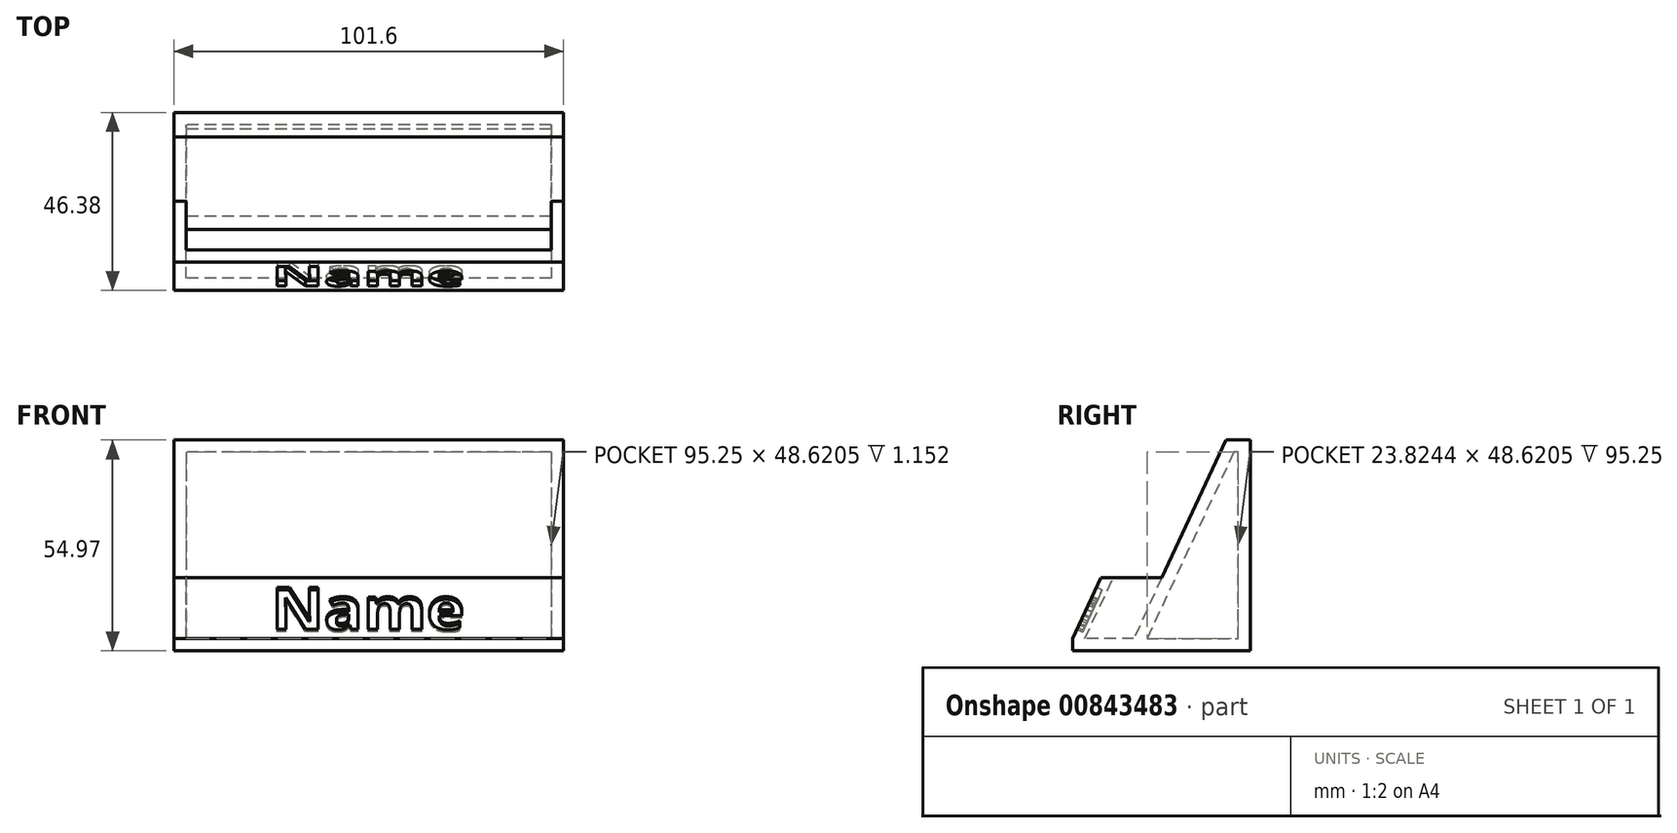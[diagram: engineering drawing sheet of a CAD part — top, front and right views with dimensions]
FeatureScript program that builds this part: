
annotation { "Feature Type Name" : "Feature", "Feature Type Description" : "" }
export const myFeature = defineFeature(function(context is Context, id is Id, definition is map)
    precondition{}
    {
        {
            var Q0;
            Q0=qCreatedBy(makeId("Right.planeOp"),FACE);
            var sketch = newSketch(context, id + "F0", { "sketchPlane" : qUnion([Q0])});
            skLineSegment(sketch, "E0", {"start": v(0, 0) * mm, "end": v(46.38, 0) * mm});
            skLineSegment(sketch, "E1", {"start": v(46.38, 0) * mm, "end": v(46.38, 54.97) * mm});
            skLineSegment(sketch, "E2", {"start": v(46.38, 54.97) * mm, "end": v(40.03, 54.97) * mm});
            skLineSegment(sketch, "E3", {"start": v(40.03, 54.97) * mm, "end": v(15.88, 3.17) * mm});
            skLineSegment(sketch, "E4", {"start": v(15.88, 3.17) * mm, "end": v(3.18, 3.17) * mm});
            skLineSegment(sketch, "E5", {"start": v(3.17, 3.17) * mm, "end": v(10.58, 19.05) * mm});
            skLineSegment(sketch, "E6", {"start": v(0, 0) * mm, "end": v(0, 3.17) * mm});
            skLineSegment(sketch, "E7", {"start": v(0, 3.17) * mm, "end": v(7.4, 19.05) * mm});
            skLineSegment(sketch, "E8", {"start": v(7.4, 19.05) * mm, "end": v(10.58, 19.05) * mm});
            skLineSegment(sketch, "E9.0", {"start": v(42.05, 51.8) * mm, "end": v(19.38, 3.17) * mm});
            skLineSegment(sketch, "E9.1", {"start": v(43.2, 51.8) * mm, "end": v(42.05, 51.8) * mm});
            skLineSegment(sketch, "E9.2", {"start": v(43.2, 3.17) * mm, "end": v(43.2, 51.8) * mm});
            skLineSegment(sketch, "E9.3", {"start": v(19.38, 3.17) * mm, "end": v(43.2, 3.17) * mm});
            skSolve(sketch);
        }
        {
            var Q0;
            Q0 = qSketchRegion(id + "F0", true);
            extrude(context, id + "F1", {"entities" : qUnion([Q0]), "endBound" : BoundingType.SYMMETRIC, "depth" : 95.25 * mm, "offsetDistance" : 25.4 * mm});
        }
        {
            var Q0;
            Q0=makeQuery(id+"F1.opExtrude","CAP_FACE",FACE,{"disambiguationData":[OSD([sQuery(id+"F0.wireOp",EDGE,"E0"),sQuery(id+"F0.wireOp",EDGE,"E1"),sQuery(id+"F0.wireOp",EDGE,"E2"),sQuery(id+"F0.wireOp",EDGE,"E3"),sQuery(id+"F0.wireOp",EDGE,"E4"),sQuery(id+"F0.wireOp",EDGE,"E5"),sQuery(id+"F0.wireOp",EDGE,"E6"),sQuery(id+"F0.wireOp",EDGE,"E7"),sQuery(id+"F0.wireOp",EDGE,"E8"),sQuery(id+"F0.wireOp",EDGE,"E9.0"),sQuery(id+"F0.wireOp",EDGE,"E9.1"),sQuery(id+"F0.wireOp",EDGE,"E9.2"),sQuery(id+"F0.wireOp",EDGE,"E9.3")])],"isStart":false});
            var sketch = newSketch(context, id + "F2", { "sketchPlane" : qUnion([Q0])});
            skLineSegment(sketch, "E10", {"start": v(7.4, 19.05) * mm, "end": v(0, 3.17) * mm});
            skLineSegment(sketch, "E11", {"start": v(0, 3.17) * mm, "end": v(0, 0) * mm});
            skLineSegment(sketch, "E12", {"start": v(0, 0) * mm, "end": v(46.38, 0) * mm});
            skLineSegment(sketch, "E13", {"start": v(46.38, 0) * mm, "end": v(46.38, 54.97) * mm});
            skLineSegment(sketch, "E14", {"start": v(46.38, 54.97) * mm, "end": v(40.03, 54.97) * mm});
            skLineSegment(sketch, "E15", {"start": v(40.03, 54.97) * mm, "end": v(23.28, 19.05) * mm});
            skLineSegment(sketch, "E16", {"start": v(23.28, 19.05) * mm, "end": v(7.4, 19.05) * mm});
            skSolve(sketch);
        }
        {
            var Q0;
            Q0 = qSketchRegion(id + "F2", true);
            extrude(context, id + "F3", {"entities" : qUnion([Q0]), "operationType" : NewBodyOperationType.ADD, "depth" : 3.17 * mm, "offsetDistance" : 25.4 * mm});
        }
        {
            var Q0;
            Q0=makeQuery(id+"F1.opExtrude","CAP_FACE",FACE,{"disambiguationData":[OSD([sQuery(id+"F0.wireOp",EDGE,"E0"),sQuery(id+"F0.wireOp",EDGE,"E1"),sQuery(id+"F0.wireOp",EDGE,"E2"),sQuery(id+"F0.wireOp",EDGE,"E3"),sQuery(id+"F0.wireOp",EDGE,"E4"),sQuery(id+"F0.wireOp",EDGE,"E5"),sQuery(id+"F0.wireOp",EDGE,"E6"),sQuery(id+"F0.wireOp",EDGE,"E7"),sQuery(id+"F0.wireOp",EDGE,"E8"),sQuery(id+"F0.wireOp",EDGE,"E9.0"),sQuery(id+"F0.wireOp",EDGE,"E9.1"),sQuery(id+"F0.wireOp",EDGE,"E9.2"),sQuery(id+"F0.wireOp",EDGE,"E9.3")])],"isStart":true});
            var sketch = newSketch(context, id + "F4", { "sketchPlane" : qUnion([Q0])});
            skLineSegment(sketch, "E17", {"start": v(-7.4, 19.05) * mm, "end": v(0, 3.17) * mm});
            skLineSegment(sketch, "E18", {"start": v(0, 3.17) * mm, "end": v(0, 0) * mm});
            skLineSegment(sketch, "E19", {"start": v(0, 0) * mm, "end": v(-46.38, 0) * mm});
            skLineSegment(sketch, "E20", {"start": v(-46.38, 0) * mm, "end": v(-46.38, 54.97) * mm});
            skLineSegment(sketch, "E21", {"start": v(-46.38, 54.97) * mm, "end": v(-40.03, 54.97) * mm});
            skLineSegment(sketch, "E22", {"start": v(-40.03, 54.97) * mm, "end": v(-23.28, 19.05) * mm});
            skLineSegment(sketch, "E23", {"start": v(-23.28, 19.05) * mm, "end": v(-7.4, 19.05) * mm});
            skSolve(sketch);
        }
        {
            var Q0;
            Q0 = qSketchRegion(id + "F4", true);
            extrude(context, id + "F5", {"entities" : qUnion([Q0]), "operationType" : NewBodyOperationType.ADD, "depth" : 3.17 * mm, "offsetDistance" : 25.4 * mm});
        }
        {
            var Q0;
            Q0=makeQuery(id+"F5.boolean.opBoolean","MERGE",FACE,{"derivedFrom":[makeQuery(id+"F3.boolean.opBoolean","MERGE",FACE,{"derivedFrom":[makeQuery(id+"F1.opExtrude","SWEPT_FACE",FACE,{"disambiguationData":[OSD([sQuery(id+"F0.wireOp",EDGE,"E7")])]}),makeQuery(id+"F3.opExtrude","SWEPT_FACE",FACE,{"disambiguationData":[OSD([sQuery(id+"F2.wireOp",EDGE,"E10")])]})]}),makeQuery(id+"F5.opExtrude","SWEPT_FACE",FACE,{"disambiguationData":[OSD([sQuery(id+"F4.wireOp",EDGE,"E17")])]})]});
            var sketch = newSketch(context, id + "F6", { "sketchPlane" : qUnion([Q0])});
            skText(sketch, "E24", { "text": "Name", "fontName": "OpenSans-Bold.ttf"});
            skPoint(sketch, "E25", {"position": v(0, 11.64) * mm});
            skLineSegment(sketch, "E26", {"start": v(-25.4, 11.64) * mm, "end": v(-50.8, 11.64) * mm, "construction": true});
            skLineSegment(sketch, "E27", {"start": v(25.4, 11.64) * mm, "end": v(50.8, 11.64) * mm, "construction": true});
            skLineSegment(sketch, "E28", {"start": v(0, 17.7) * mm, "end": v(0, 20.4) * mm, "construction": true});
            skLineSegment(sketch, "E29", {"start": v(0, 5.56) * mm, "end": v(0, 2.88) * mm, "construction": true});
            const initialGuessF6  = {"E24": [-0.0254, 0.00556, 1, 0, 0.01215]};
            skSetInitialGuess(sketch, initialGuessF6);
            skSolve(sketch);
        }
        {
            var Q0;
            Q0 = qSketchRegion(id + "F6", true);
            extrude(context, id + "F7", {"entities" : qUnion([Q0]), "operationType" : NewBodyOperationType.REMOVE, "oppositeDirection" : true, "depth" : 1.59 * mm, "offsetDistance" : 25.4 * mm});
        }
    });
